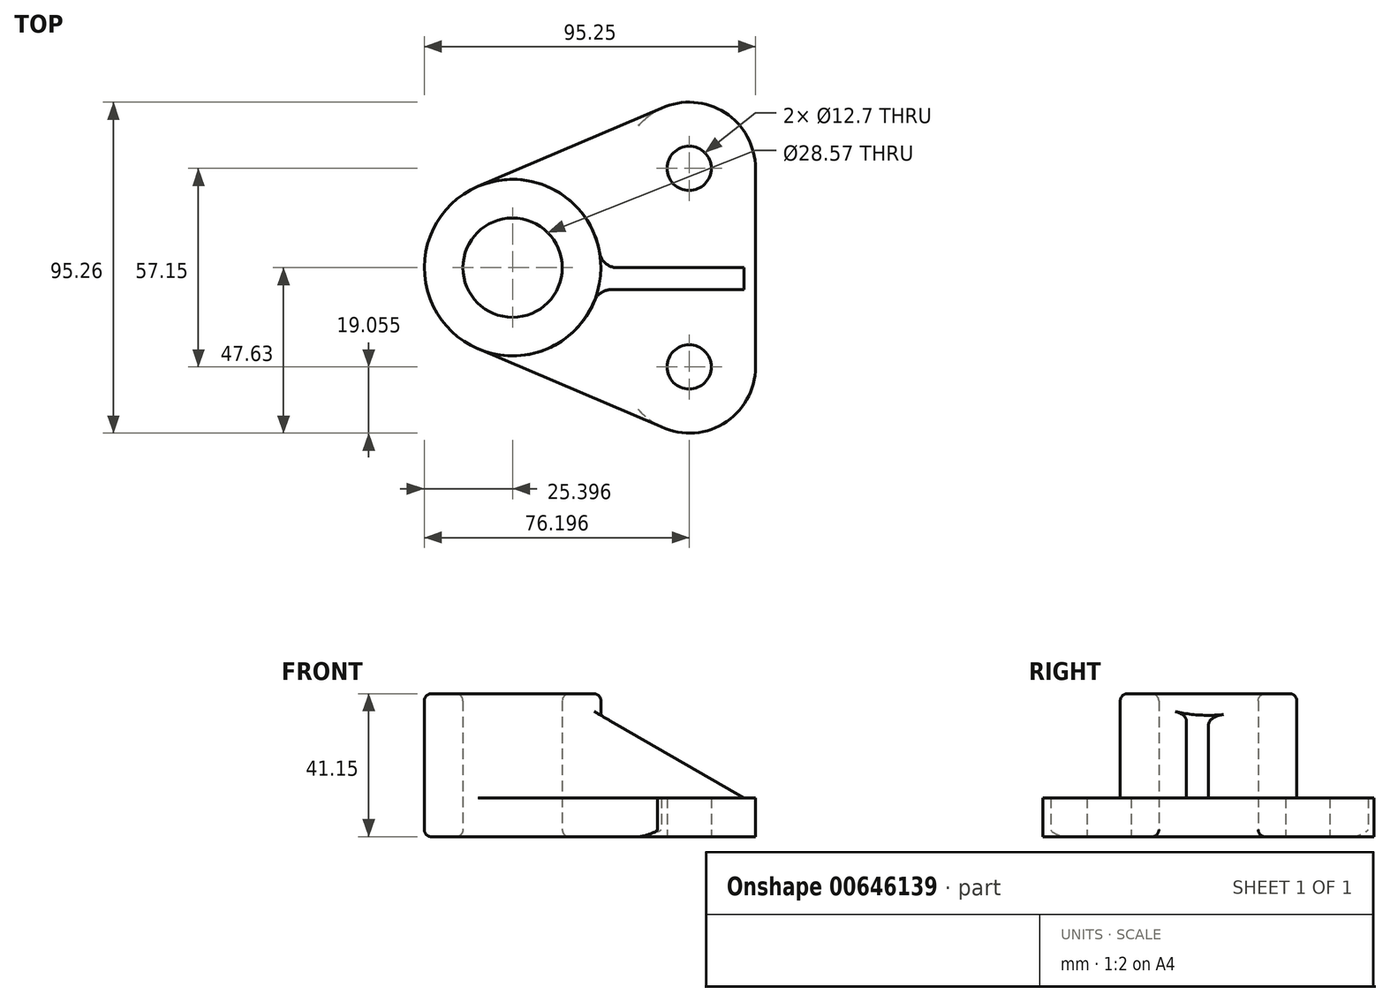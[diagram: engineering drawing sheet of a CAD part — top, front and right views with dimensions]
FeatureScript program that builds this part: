
annotation { "Feature Type Name" : "Feature", "Feature Type Description" : "" }
export const myFeature = defineFeature(function(context is Context, id is Id, definition is map)
    precondition{}
    {
        {
            var Q0;
            Q0=qCreatedBy(makeId("Top.planeOp"),FACE);
            var sketch = newSketch(context, id + "F0", { "sketchPlane" : qUnion([Q0])});
            skLineSegment(sketch, "E0", {"start": v(-42.84, 0) * mm, "end": v(7.96, 0) * mm});
            skLineSegment(sketch, "E1", {"start": v(7.96, 0) * mm, "end": v(7.96, -28.58) * mm});
            skLineSegment(sketch, "E2", {"start": v(7.96, 0) * mm, "end": v(7.96, 0) * mm});
            skLineSegment(sketch, "E3", {"start": v(7.96, 0) * mm, "end": v(7.96, 28.58) * mm});
            skCircle(sketch, "E4", {"center": v(-42.84, 0) * mm, "radius": 14.29 * mm});
            skCircle(sketch, "E5", {"center": v(-42.84, 0) * mm, "radius": 25.4 * mm});
            skCircle(sketch, "E6", {"center": v(7.96, 28.58) * mm, "radius": 19.05 * mm});
            skCircle(sketch, "E7", {"center": v(7.96, -28.58) * mm, "radius": 19.05 * mm});
            skCircle(sketch, "E8", {"center": v(7.96, 28.58) * mm, "radius": 6.35 * mm});
            skCircle(sketch, "E9", {"center": v(7.96, -28.58) * mm, "radius": 6.35 * mm});
            skLineSegment(sketch, "E10", {"start": v(-52.81, 23.36) * mm, "end": v(0, 45.88) * mm});
            skLineSegment(sketch, "E11", {"start": v(-52.78, -23.38) * mm, "end": v(-1.13, -45.32) * mm});
            skLineSegment(sketch, "E12", {"start": v(27, 28.58) * mm, "end": v(27, -28.58) * mm});
            skSolve(sketch);
        }
        {
            var Q0;
            Q0=makeQuery(id+"F0.imprint","IMPRINT",FACE,{"disambiguationData":[TD([[makeQuery(id+"F0.imprint","IMPRINT",EDGE,{"derivedFrom":sQuery(id+"F0.wireOp",EDGE,"E4")}),-1.0]])]});
            extrude(context, id + "F1", {"entities" : qUnion([Q0]), "depth" : 41.15 * mm, "offsetDistance" : 25.4 * mm});
        }
        {
            var Q0;
            {var subQ0=sQuery(id+"F0.wireOp",EDGE,"E11");Q0=makeQuery(id+"F0.imprint","IMPRINT",FACE,{"disambiguationData":[TD([[makeQuery(id+"F0.imprint","IMPRINT",EDGE,{"derivedFrom":subQ0}),1.0]])]});}
            var Q1;
            {var subQ0=sQuery(id+"F0.wireOp",EDGE,"E10");Q1=makeQuery(id+"F0.imprint","IMPRINT",FACE,{"disambiguationData":[TD([[makeQuery(id+"F0.imprint","IMPRINT",EDGE,{"derivedFrom":subQ0}),-1.0]])]});}
            var Q2;
            Q2=makeQuery(id+"F0.imprint","IMPRINT",FACE,{"disambiguationData":[TD([[makeQuery(id+"F0.imprint","IMPRINT",EDGE,{"derivedFrom":sQuery(id+"F0.wireOp",EDGE,"E8")}),-1.0]])]});
            var Q3;
            {var subQ0=sQuery(id+"F0.wireOp",EDGE,"E12");Q3=makeQuery(id+"F0.imprint","IMPRINT",FACE,{"disambiguationData":[TD([[makeQuery(id+"F0.imprint","IMPRINT",EDGE,{"derivedFrom":subQ0}),-1.0]])]});}
            var Q4;
            Q4=makeQuery(id+"F0.imprint","IMPRINT",FACE,{"disambiguationData":[TD([[makeQuery(id+"F0.imprint","IMPRINT",EDGE,{"derivedFrom":sQuery(id+"F0.wireOp",EDGE,"E9")}),-1.0]])]});
            extrude(context, id + "F2", {"entities" : qUnion([Q0, Q1, Q2, Q3, Q4]), "operationType" : NewBodyOperationType.ADD, "depth" : 11.18 * mm, "offsetDistance" : 25.4 * mm});
        }
        {
            var Q0;
            Q0=qCreatedBy(makeId("Front.planeOp"),FACE);
            var sketch = newSketch(context, id + "F3", { "sketchPlane" : qUnion([Q0])});
            skLineSegment(sketch, "E13.0.1", {"start": v(27, 0) * mm, "end": v(27, 11.18) * mm});
            skLineSegment(sketch, "E13.0.3", {"start": v(27, 11.18) * mm, "end": v(27, 0) * mm});
            skLineSegment(sketch, "E14", {"start": v(27, 11.18) * mm, "end": v(23.7, 11.18) * mm});
            skLineSegment(sketch, "E15", {"start": v(23.7, 11.18) * mm, "end": v(-19.65, 36.2) * mm});
            skLineSegment(sketch, "E16", {"start": v(-19.65, 36.2) * mm, "end": v(-19.65, 11.18) * mm});
            skLineSegment(sketch, "E17", {"start": v(-19.65, 11.18) * mm, "end": v(23.7, 11.18) * mm});
            skSolve(sketch);
        }
        {
            var Q0;
            Q0=makeQuery(id+"F3.imprint","IMPRINT",FACE,{"disambiguationData":[TD([[makeQuery(id+"F3.imprint","IMPRINT",EDGE,{"derivedFrom":sQuery(id+"F3.wireOp",EDGE,"E15")}),1.0]])]});
            extrude(context, id + "F4", {"entities" : qUnion([Q0]), "operationType" : NewBodyOperationType.ADD, "depth" : 6.35 * mm, "offsetDistance" : 25.4 * mm});
        }
        {
            var Q0;
            Q0=makeQuery(id+"F1.opExtrude","CAP_EDGE",EDGE,{"disambiguationData":[OSD([sQuery(id+"F0.wireOp",EDGE,"E4")])],"isStart":true});
            fillet(context, id + "F5", {"entities" : qUnion([Q0]), "radius" : 2.03 * mm, "tangentPropagation" : true, "allowEdgeOverflow" : false});
        }
        {
            var Q0;
            Q0=makeQuery(id+"F1.opExtrude","CAP_EDGE",EDGE,{"disambiguationData":[OSD([sQuery(id+"F0.wireOp",EDGE,"E5")])],"isStart":true});
            fillet(context, id + "F6", {"entities" : qUnion([Q0]), "radius" : 2.03 * mm, "tangentPropagation" : true, "allowEdgeOverflow" : false});
        }
        {
            var Q0;
            Q0=makeQuery(id+"F1.opExtrude","CAP_FACE",FACE,{"disambiguationData":[OSD([sQuery(id+"F0.wireOp",EDGE,"E4"),sQuery(id+"F0.wireOp",EDGE,"E5")])],"isStart":false});
            fillet(context, id + "F7", {"entities" : qUnion([Q0]), "radius" : 2.03 * mm, "tangentPropagation" : true, "allowEdgeOverflow" : false});
        }
        {
            var Q0;
            {var subQ0=sQuery(id+"F0.wireOp",EDGE,"E5");var subQ1=sQuery(id+"F0.wireOp",EDGE,"E11");Q0=makeQuery(id+"F4.boolean.opBoolean","SPLIT",EDGE,{"disambiguationData":[TD([makeQuery(id+"F2.opExtrude","SWEPT_FACE",FACE,{"disambiguationData":[OSD([subQ1])]})])],"derivedFrom":makeQuery(id+"F2.opExtrude","CAP_EDGE",EDGE,{"disambiguationData":[OSD([subQ0])],"isStart":false})});}
            var Q1;
            Q1=makeQuery(id+"F4.opExtrude","CAP_EDGE",EDGE,{"disambiguationData":[OSD([sQuery(id+"F3.wireOp",EDGE,"E17")])],"isStart":false});
            var Q2;
            Q2=makeQuery(id+"F4.boolean.opBoolean","INTERSECT",EDGE,{"derivedFrom":[makeQuery(id+"F1.opExtrude","SWEPT_FACE",FACE,{"disambiguationData":[OSD([sQuery(id+"F0.wireOp",EDGE,"E5")])]}),makeQuery(id+"F4.opExtrude","CAP_FACE",FACE,{"disambiguationData":[OSD([sQuery(id+"F3.wireOp",EDGE,"E15"),sQuery(id+"F3.wireOp",EDGE,"E16"),sQuery(id+"F3.wireOp",EDGE,"E17")])],"isStart":false})]});
            var Q3;
            Q3=makeQuery(id+"F4.boolean.opBoolean","INTERSECT",EDGE,{"derivedFrom":[makeQuery(id+"F1.opExtrude","SWEPT_FACE",FACE,{"disambiguationData":[OSD([sQuery(id+"F0.wireOp",EDGE,"E5")])]}),makeQuery(id+"F4.opExtrude","CAP_FACE",FACE,{"disambiguationData":[OSD([sQuery(id+"F3.wireOp",EDGE,"E15"),sQuery(id+"F3.wireOp",EDGE,"E16"),sQuery(id+"F3.wireOp",EDGE,"E17")])],"isStart":true})]});
            var Q4;
            {var subQ0=sQuery(id+"F0.wireOp",EDGE,"E5");var subQ1=sQuery(id+"F0.wireOp",EDGE,"E10");Q4=makeQuery(id+"F4.boolean.opBoolean","SPLIT",EDGE,{"disambiguationData":[TD([makeQuery(id+"F2.opExtrude","SWEPT_FACE",FACE,{"disambiguationData":[OSD([subQ1])]})])],"derivedFrom":makeQuery(id+"F2.opExtrude","CAP_EDGE",EDGE,{"disambiguationData":[OSD([subQ0])],"isStart":false})});}
            var Q5;
            Q5=makeQuery(id+"F4.opExtrude","CAP_EDGE",EDGE,{"disambiguationData":[OSD([sQuery(id+"F3.wireOp",EDGE,"E17")])],"isStart":true});
            fillet(context, id + "F8", {"entities" : qUnion([Q0, Q1, Q2, Q3, Q4, Q5]), "radius" : 5.08 * mm, "tangentPropagation" : true, "allowEdgeOverflow" : false});
        }
    });
